# Revit family: ADB Chef’s sink cupboard CMA 801
name_source: partatom
category: Equipement spécialisé
units: mm (PartAtom-declared; Revit-internal decimal feet)

## family parameters
Basée sur le plan de construction = Non
Conserver l'orientation des annotations = Non
Cote de connecteur circulaire = Utiliser le diamètre
Couper avec des vides une fois chargée = Non
Numéro OmniClass = 23.40.40.14.17.11
Partagée = Non
Repère de localisation dans la pièce = Non
Titre OmniClass = Cookers, Ovens, Stoves
Toujours verticalement = Oui
Type d'élément = Normal

## types (2) — shared parameters
Commentaires du type = Ambassade range - Cupboards - Worktops
Direct Waste Size = 40.00 mm
Fabricant = Société Industrielle de Lacanche
URL = https://www.ambassade-de-bourgogne.com
URL Cutsheet = https://www.ambassade-de-bourgogne.com
zero-valued in all types: Elévation par défaut

## per-type parameters (varying)
| type | Description | Plaque |
| CMA 801 BCFG | Left hs Chef’s sink | CME801 BCFG_BCFD : BCFG |
| CMA 801 BCFD | Right hs Chef’s sink | CME801 BCFG_BCFD : BCFD |

note: column(s) folded — value = type name in every type: Modèle
